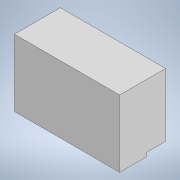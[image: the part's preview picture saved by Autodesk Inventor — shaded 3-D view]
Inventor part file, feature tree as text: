
AUTODESK INVENTOR PART (.ipt)
format: ipt  version: 2021 (Build 250183000, 183)  size: 96,768 bytes
history: native  units: mm
features: extrude x2, sketch x2, other x1
ambient origin geometry x8: Origin, YZ Plane, XZ Plane, XY Plane, X Axis, Y Axis, Z Axis, Center Point
bodies: Body1 (feature_tree)
feature tree (5):
  other  "Sólido1"
  extrude  "Extrusão1"  Depth=24.0mm
  extrude  "Extrusão2"  Depth=10.0mm
  sketch  "Esboço1"  dims[d0=35.0mm d1=24.0mm]
  sketch  "Esboço2"  dims[d2=55.0mm d3=0.0mm d4=10.0mm d5=2.0mm d6=0.0mm]
